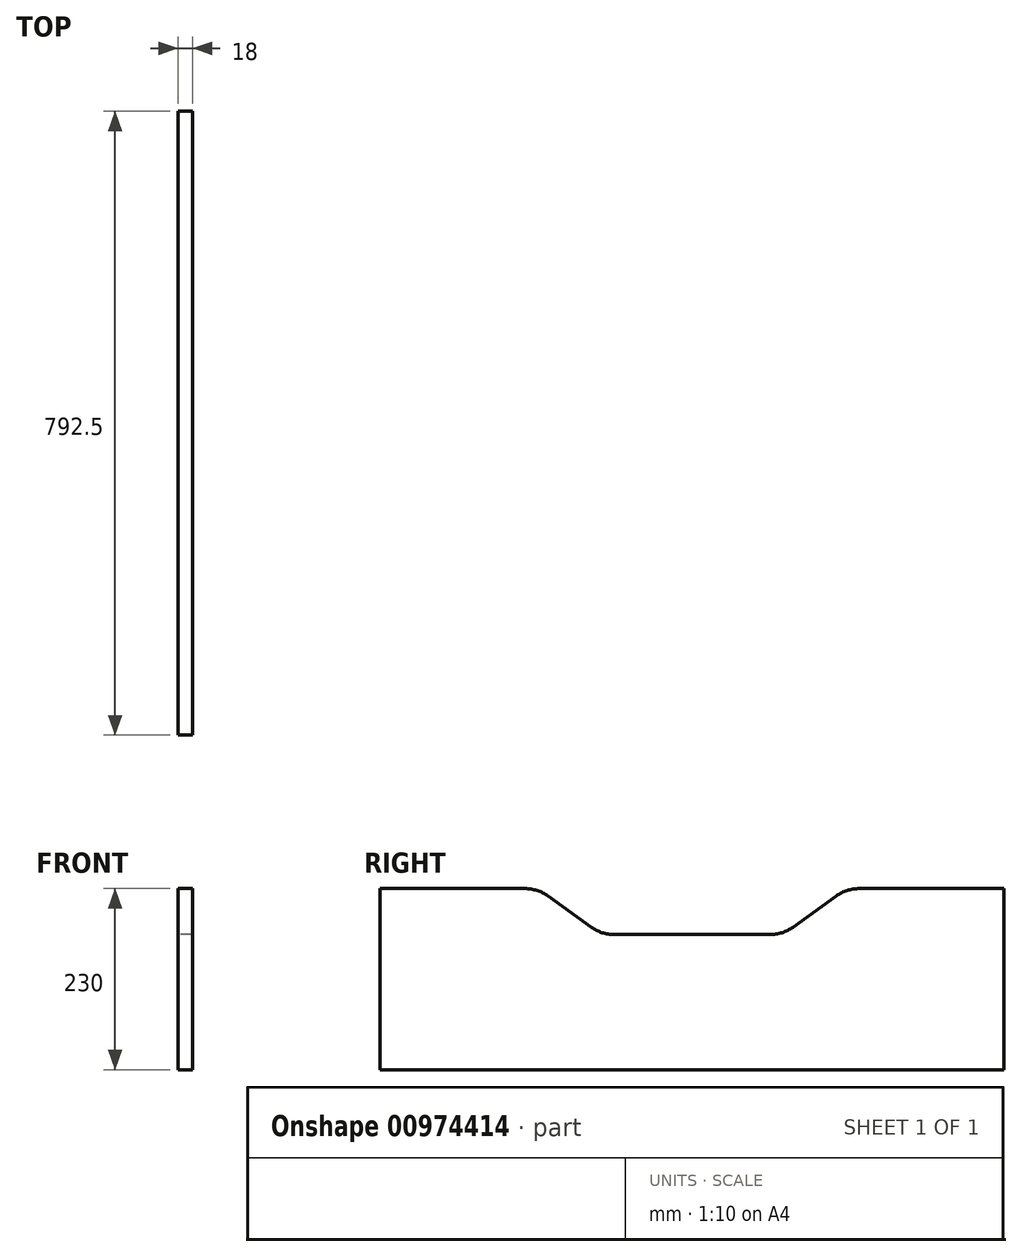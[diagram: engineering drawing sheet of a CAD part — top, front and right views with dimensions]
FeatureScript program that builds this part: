
annotation { "Feature Type Name" : "Feature", "Feature Type Description" : "" }
export const myFeature = defineFeature(function(context is Context, id is Id, definition is map)
    precondition{}
    {
        {
            var Q0;
            Q0=qCreatedBy(makeId("Right.planeOp"),FACE);
            var sketch = newSketch(context, id + "F0", { "sketchPlane" : qUnion([Q0])});
            skLineSegment(sketch, "E0.bottom", {"start": v(396.25, 115) * mm, "end": v(-396.25, 115) * mm});
            skLineSegment(sketch, "E0.top", {"start": v(396.25, -115) * mm, "end": v(-396.25, -115) * mm});
            skLineSegment(sketch, "E0.left", {"start": v(396.25, 115) * mm, "end": v(396.25, -115) * mm});
            skLineSegment(sketch, "E0.right", {"start": v(-396.25, 115) * mm, "end": v(-396.25, -115) * mm});
            skPoint(sketch, "E0.middle", {"position": v(0, 0) * mm});
            skLineSegment(sketch, "E1", {"start": v(396.25, 115) * mm, "end": v(212.36, 115) * mm});
            skLineSegment(sketch, "E2", {"start": v(183.17, 105.6) * mm, "end": v(128.14, 66.03) * mm});
            skLineSegment(sketch, "E3", {"start": v(98.95, 56.62) * mm, "end": v(-98.95, 56.62) * mm});
            skLineSegment(sketch, "E4", {"start": v(-128.14, 66.03) * mm, "end": v(-183.17, 105.6) * mm});
            skLineSegment(sketch, "E5", {"start": v(-212.36, 115) * mm, "end": v(-396.25, 115) * mm});
            skPoint(sketch, "E6.visualSharp", {"position": v(196.25, 115) * mm});
            skArc(sketch, "E6.filletArc", {"start": v(212.36, 115) * mm, "mid": v(197.03, 112.6) * mm, "end": v(183.17, 105.6) * mm});
            skPoint(sketch, "E7.visualSharp", {"position": v(115.06, 56.62) * mm});
            skArc(sketch, "E7.filletArc", {"start": v(98.95, 56.62) * mm, "mid": v(114.28, 59.03) * mm, "end": v(128.14, 66.03) * mm});
            skPoint(sketch, "E8.visualSharp", {"position": v(-115.06, 56.62) * mm});
            skArc(sketch, "E8.filletArc", {"start": v(-128.14, 66.03) * mm, "mid": v(-114.28, 59.03) * mm, "end": v(-98.95, 56.62) * mm});
            skPoint(sketch, "E9.visualSharp", {"position": v(-196.25, 115) * mm});
            skArc(sketch, "E9.filletArc", {"start": v(-183.17, 105.6) * mm, "mid": v(-197.03, 112.6) * mm, "end": v(-212.36, 115) * mm});
            skSolve(sketch);
        }
        {
            var Q0;
            Q0=makeQuery(id+"F0.imprint","IMPRINT",FACE,{"disambiguationData":[TD([[makeQuery(id+"F0.imprint","IMPRINT",EDGE,{"derivedFrom":sQuery(id+"F0.wireOp",EDGE,"E0.top")}),-1.0]])]});
            extrude(context, id + "F1", {"entities" : qUnion([Q0]), "depth" : 18 * mm, "offsetDistance" : 25 * mm});
        }
    });
